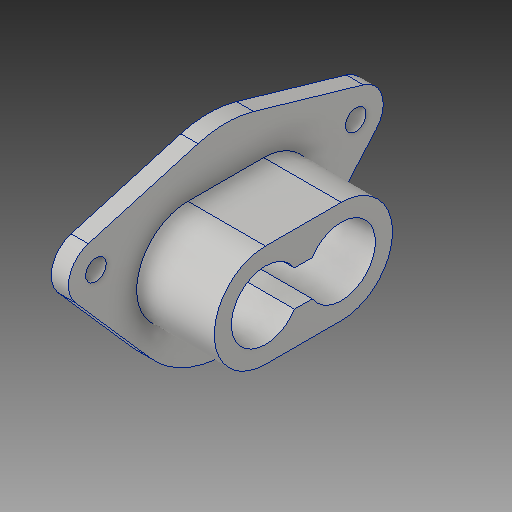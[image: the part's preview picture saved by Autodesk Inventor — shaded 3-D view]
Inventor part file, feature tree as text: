
AUTODESK INVENTOR PART (.ipt)
format: ipt  version: 2019 (Build 230136000, 136)  size: 189,440 bytes
history: native  units: in
note: dims shown in document units (in); Inventor stores cm internally (conversion verified against a paired STEP export)
features: extrude x2, sketch x1, projected_geometry x1
ambient origin geometry x8: Origin, YZ Plane, XZ Plane, XY Plane, X Axis, Y Axis, Z Axis, Center Point
bodies: Solid1 (feature_tree)
feature tree (4):
  extrude  "Extrusion6"  Depth=0.564in
  extrude  "Extrusion7"  Depth=0.564in
  sketch  "Sketch6"  dims[d5=1.4567in d6=0.8in d47=0.15in d48=0.15in d49=1.456in d50=0.276in d51=0.276in d52=0.945in d53=0.945in d54=0.4in d55=0.4in d56=0.495in d57=0.495in d58=0.5512in d59=90.0deg d60=90.0deg d61=0.728in d62=0.728in d63=0.2756in d64=0.2756in d71=0.26in d72=0.13in d73=0.125in d74=0.0in d75=0.2475in d76=0.2475in d77=0.745in d78=0.745in d79=0.564in d80=0.0in]
  projected_geometry  "Projected Loop5"
